FCSTD DOCUMENT  (FreeCAD 0.21R33771 (Git))
Label: Slabbed_Card_Frame
License: All rights reserved
LicenseURL: http://en.wikipedia.org/wiki/All_rights_reserved
objects: Spreadsheet::Sheet×1

FEATURE [Spreadsheet::Sheet] Spreadsheet  label="prams"
  cells = A1='Frame; A2='frame_width; B2(frame_width)=186; C2='Needs to be 10mm > Card Window Width; A3='frame_length; B3(frame_length)=240; C3='Needs to be 10mm > Card Window Length; A4='frame_bordered_pocket_width; B4(frame_bordered_pocket_width)==B2 - 30; C4='Calculated - Do Not Change; A5='frame_bordered__pocket_length; B5(frame_bordered__pocket_length)==B3 - 30; C5='Calculated - Do Not Change; A6='frame_border_pocket_depth; B6(frame_border_pocket_depth)=30; A7='frame_border_pocket_depth_minimum; B7(frame_border_pocket_depth_minimum)=11; A8='frame_border_chamfer_degrees; B8(frame_border_chamfer_degrees)=10; D9=1; E9=2; F9=3; A10='Slabbed Card Window; D10='PSA Normal Card; E10='PSA Topps Giants; F10='GEM Normal Card; A11='card_window_width; B11(card_window_width)=80.32; D11=80.32; A12='card_window_length; B12(card_window_length)=135.5; D12=135.5; A13='card_window_depth; B13(card_window_depth)=6.4; D13=6.4; A14='card_window_border_height; B14(card_window_border_height)=4; A15='card_window_border_chamfer_degrees; B15(card_window_border_chamfer_degrees)==B14 - 1.5; C15='Calculated - Do Not Change
